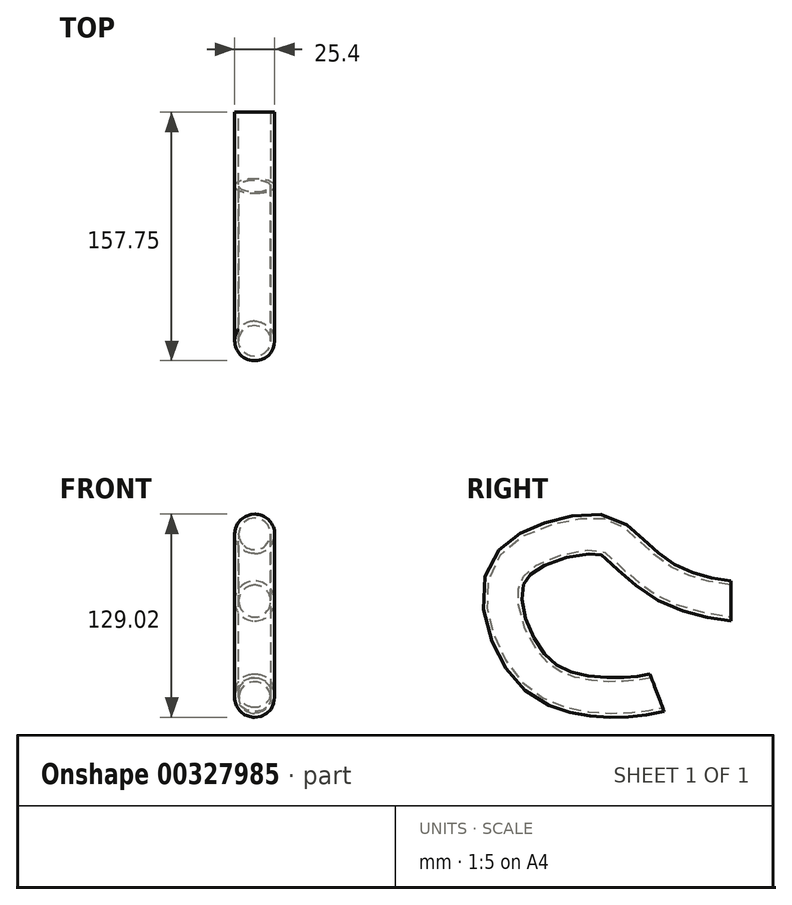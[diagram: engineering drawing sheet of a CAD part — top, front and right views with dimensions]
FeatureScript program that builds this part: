
annotation { "Feature Type Name" : "Feature", "Feature Type Description" : "" }
export const myFeature = defineFeature(function(context is Context, id is Id, definition is map)
    precondition{}
    {
        {
            var Q0;
            Q0=qCreatedBy(makeId("Front.planeOp"),FACE);
            var sketch = newSketch(context, id + "F0", { "sketchPlane" : qUnion([Q0])});
            skCircle(sketch, "E0", {"center": v(0, 0) * mm, "radius": 12.7 * mm});
            skSolve(sketch);
        }
        {
            var Q0;
            Q0=qCreatedBy(makeId("Right.planeOp"),FACE);
            var sketch = newSketch(context, id + "F1", { "sketchPlane" : qUnion([Q0])});
            skFitSpline(sketch, "E1", {"points": [v(0, 0) * mm, v(-39.53, 11.06) * mm, v(-69.9, 35.3) * mm, v(-85.9, 42.6) * mm, v(-134.37, 27.3) * mm, v(-144.49, -5.18) * mm, v(-124.02, -45.65) * mm, v(-93.19, -59.77) * mm, v(-62.36, -60.71) * mm, v(-46.83, -58.12) * mm], "startDerivative": vector(-330.15, 51.9) * mm, "endDerivative": vector(184.12, 39.29) * mm});
            skSolve(sketch);
        }
        {
            var Q0;
            Q0=makeQuery(id+"F0.imprint","IMPRINT",FACE,{"disambiguationData":[TD([[makeQuery(id+"F0.imprint","IMPRINT",EDGE,{"derivedFrom":sQuery(id+"F0.wireOp",EDGE,"E0")}),1.0]])]});
            var Q1;
            Q1=sQuery(id+"F1.wireOp",EDGE,"E1");
            sweep(context, id + "F2", {"profiles" : qUnion([Q0]), "path" : qUnion([Q1])});
        }
        {
            var Q0;
            Q0=makeQuery(id+"F2.opSweep","CAP_FACE",FACE,{"disambiguationData":[OSD([sQuery(id+"F0.wireOp",EDGE,"E0"),sQuery(id+"F1.wireOp",VERTEX,"E1.start")])],"isStart":true});
            var Q1;
            Q1=makeQuery(id+"F2.opSweep","CAP_FACE",FACE,{"disambiguationData":[OSD([sQuery(id+"F0.wireOp",EDGE,"E0"),sQuery(id+"F1.wireOp",VERTEX,"E1.end")])],"isStart":false});
            shell(context, id + "F3", {"entities" : qUnion([Q0, Q1]), "thickness" : 2.54 * mm});
        }
    });
